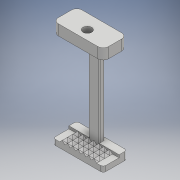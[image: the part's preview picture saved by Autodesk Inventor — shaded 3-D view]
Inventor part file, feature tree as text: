
AUTODESK INVENTOR PART (.ipt)
format: ipt  version: 2017 (Build 210142000, 142)  size: 269,824 bytes
history: native  units: mm
features: extrude x9, sketch x8, fillet x3, chamfer x2, projected_geometry x2
ambient origin geometry x8: Origin, YZ Plane, XZ Plane, XY Plane, X Axis, Y Axis, Z Axis, Center Point
bodies: Solid1 (feature_tree)
feature tree (24):
  extrude  "Extrusion1"  Depth=9.0mm
  extrude  "Extrusion2"  Depth=2.0mm
  sketch  "Sketch6"  dims[d5=2.0mm d6=1.5mm d7=0.0mm]
  extrude  "Extrusion5"  Depth=2.0mm TaperAngle=0.0deg
  extrude  "Extrusion6"  Depth=4.0mm TaperAngle=0.0deg
  extrude  "Extrusion7"  Depth=4.0mm
  extrude  "Extrusion8"  Depth=1.0mm
  extrude  "Extrusion9"  TaperAngle=135.0deg  [1 undecoded]
  fillet  "Fillet2"  [1 undecoded]
  fillet  "Fillet3"  Radius=4.0mm
  extrude  "Extrusion10"  Depth=2.0mm
  extrude  "Extrusion11"  Depth=2.0mm
  chamfer  "Chamfer3"  Distance=6.0mm
  chamfer  "Chamfer4"  Distance=1.0mm
  fillet  "Fillet4"  Radius=2.0mm
  sketch  "Sketch1"  dims[d0=19.0mm d1=9.0mm]
  sketch  "Sketch2"  dims[d2=3.0mm d3=0.0mm d4=2.0mm]
  sketch  "Sketch7"  dims[d13=4.0mm d14=32.0mm d15=0.0mm]
  projected_geometry  "Projected Loop2"
  sketch  "Sketch8"  dims[d16=4.0mm d17=0.0mm d18=3.3mm]
  projected_geometry  "Projected Loop3"
  sketch  "Sketch10"  dims[d19=4.0mm d20=0.0mm d23=1.0mm]
  sketch  "Sketch11"  dims[d24=6.0mm d25=135.0deg d26=90.0deg d27=4.0mm d28=0.0mm]
  sketch  "Sketch12"  dims[d30=135.0deg d31=40.0mm d33=2.0mm d34=10.0mm d36=10.0mm d38=40.0mm d40=2.0mm d41=10.0mm d43=10.0mm d45=6.0mm d46=0.0mm d47=1.0mm d48=2.0mm d55=10.0mm d56=0.0mm d57=4.0mm d58=0.0mm d59=2.0mm d60=1.0mm d61=45.0deg d62=2.0mm d63=1.0mm d64=45.0deg d65=0.3mm d66=5.5mm]
note: 2 required parameter values undecoded (feature->parameter linkage not recoverable at this tier; creation-order binding heuristic only, values carry confidence <= 0.55)
